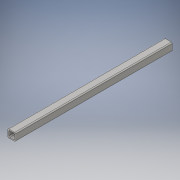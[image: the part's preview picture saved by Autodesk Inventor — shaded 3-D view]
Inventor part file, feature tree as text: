
AUTODESK INVENTOR PART (.ipt)
format: ipt  version: 2016 (Build 200138000, 138)  size: 113,664 bytes
history: native  units: in
note: dims shown in document units (in); Inventor stores cm internally (conversion verified against a paired STEP export)
features: extrude x1, sketch x1
ambient origin geometry x8: Origin, YZ Plane, XZ Plane, XY Plane, X Axis, Y Axis, Z Axis, Center Point
bodies: Solid1 (feature_tree)
feature tree (2):
  extrude  "Extrusion1"  Depth=1.0in
  sketch  "Sketch1"  dims[d0=1.0in d1=1.0in d2=0.125in d3=0.125in d4=20.0in d5=0.0in]
